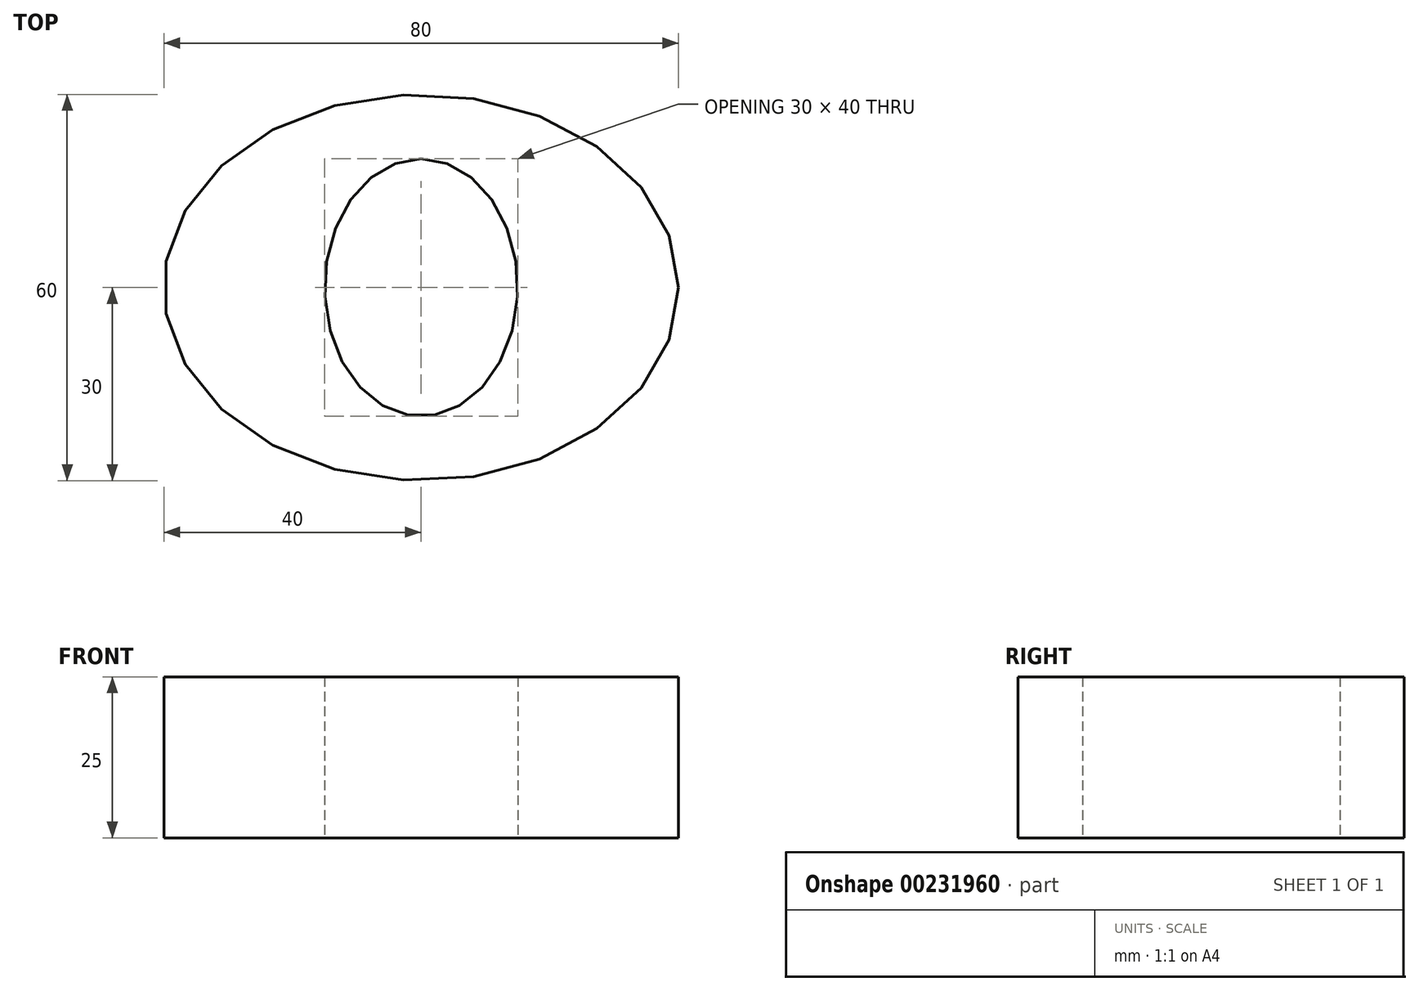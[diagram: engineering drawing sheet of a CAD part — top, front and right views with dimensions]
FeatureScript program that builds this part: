
annotation { "Feature Type Name" : "Feature", "Feature Type Description" : "" }
export const myFeature = defineFeature(function(context is Context, id is Id, definition is map)
    precondition{}
    {
        {
            var Q0;
            Q0=qCreatedBy(makeId("Top.planeOp"),FACE);
            var sketch = newSketch(context, id + "F0", { "sketchPlane" : qUnion([Q0])});
            skEllipse(sketch, "E0", {"center": v(0, 0) * mm, "majorRadius": 20 * mm, "minorRadius": 15 * mm, "majorAxis": v(0, 1)});
            skEllipse(sketch, "E1", {"center": v(0, 0) * mm, "majorRadius": 40 * mm, "minorRadius": 30 * mm, "majorAxis": v(1, 0)});
            skSolve(sketch);
        }
        {
            var Q0;
            Q0=makeQuery(id+"F0.imprint","IMPRINT",FACE,{"disambiguationData":[TD([[makeQuery(id+"F0.imprint","IMPRINT",EDGE,{"derivedFrom":sQuery(id+"F0.wireOp",EDGE,"E0")}),-1.0]])]});
            extrude(context, id + "F1", {"entities" : qUnion([Q0]), "depth" : 25 * mm});
        }
    });
